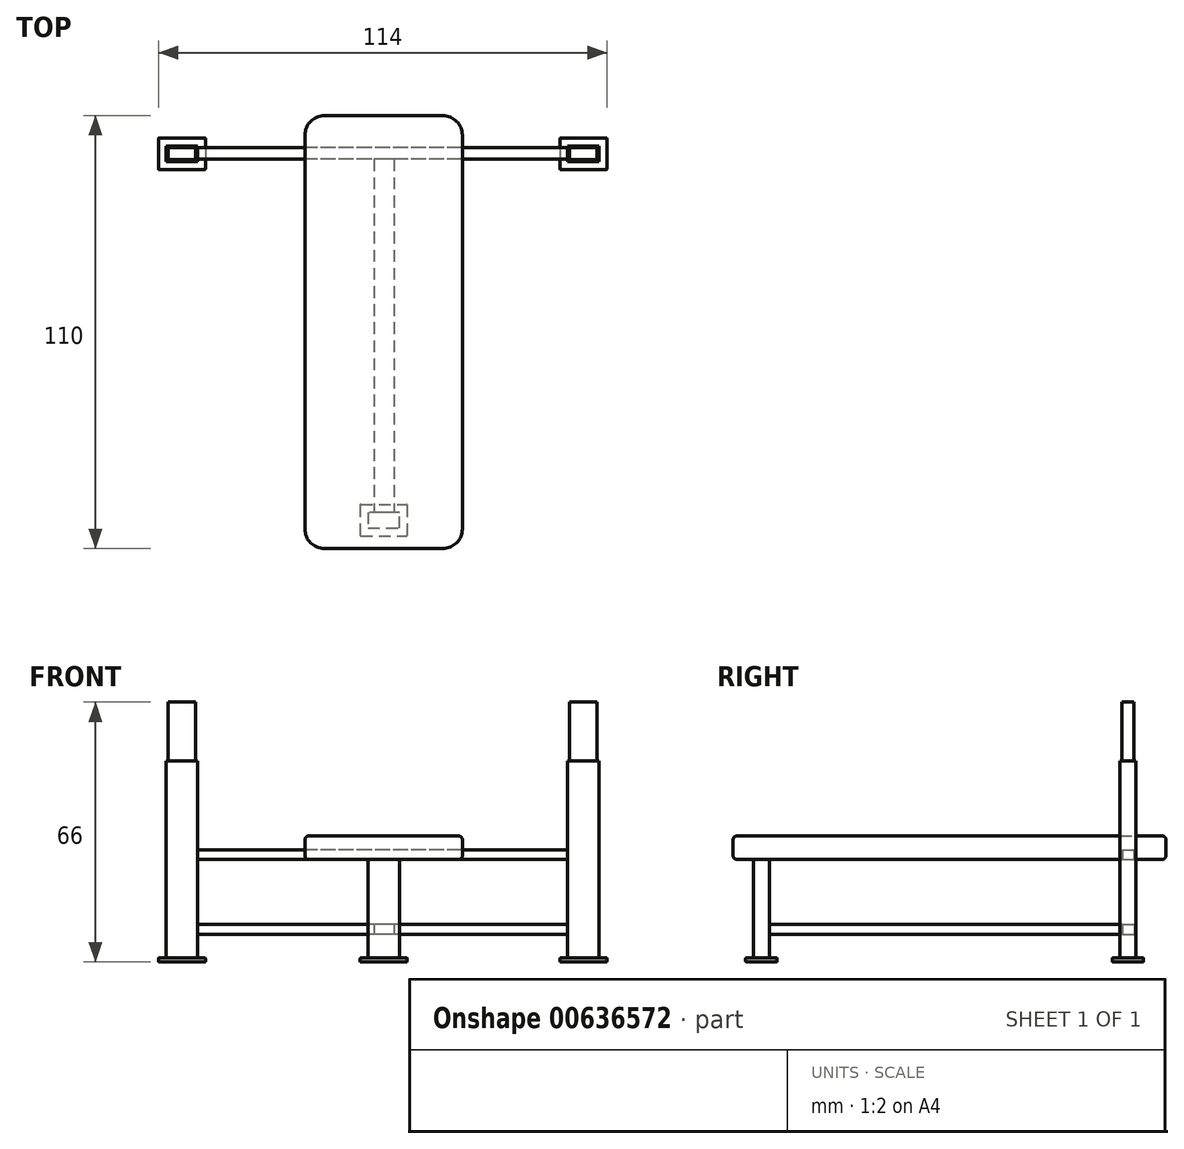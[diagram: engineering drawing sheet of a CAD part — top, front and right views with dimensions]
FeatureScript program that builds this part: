
annotation { "Feature Type Name" : "Feature", "Feature Type Description" : "" }
export const myFeature = defineFeature(function(context is Context, id is Id, definition is map)
    precondition{}
    {
        {
            var Q0;
            Q0=qCreatedBy(makeId("Top.planeOp"),FACE);
            var sketch = newSketch(context, id + "F0", { "sketchPlane" : qUnion([Q0])});
            skLineSegment(sketch, "E0.bottom", {"start": v(-5.75, -43.57) * mm, "end": v(6.25, -43.57) * mm});
            skLineSegment(sketch, "E0.top", {"start": v(-5.75, -51.57) * mm, "end": v(6.25, -51.57) * mm});
            skLineSegment(sketch, "E0.left", {"start": v(-5.75, -43.57) * mm, "end": v(-5.75, -51.57) * mm});
            skLineSegment(sketch, "E0.right", {"start": v(6.25, -43.57) * mm, "end": v(6.25, -51.57) * mm});
            skSolve(sketch);
        }
        {
            var Q0;
            Q0=qCreatedBy(makeId("Top.planeOp"),FACE);
            var sketch = newSketch(context, id + "F1", { "sketchPlane" : qUnion([Q0])});
            skLineSegment(sketch, "E1", {"start": v(0, 49.53) * mm, "end": v(0, -40.59) * mm, "construction": true});
            skLineSegment(sketch, "E2.bottom", {"start": v(45, 49.53) * mm, "end": v(57, 49.53) * mm});
            skLineSegment(sketch, "E2.top", {"start": v(45, 41.53) * mm, "end": v(57, 41.53) * mm});
            skLineSegment(sketch, "E2.left", {"start": v(45, 49.53) * mm, "end": v(45, 41.53) * mm});
            skLineSegment(sketch, "E2.right", {"start": v(57, 49.53) * mm, "end": v(57, 41.53) * mm});
            skLineSegment(sketch, "E3.bottom", {"start": v(-45, 49.53) * mm, "end": v(-57, 49.53) * mm});
            skLineSegment(sketch, "E3.top", {"start": v(-45, 41.53) * mm, "end": v(-57, 41.53) * mm});
            skLineSegment(sketch, "E3.left", {"start": v(-45, 49.53) * mm, "end": v(-45, 41.53) * mm});
            skLineSegment(sketch, "E3.right", {"start": v(-57, 49.53) * mm, "end": v(-57, 41.53) * mm});
            skSolve(sketch);
        }
        {
            var Q0;
            Q0 = qSketchRegion(id + "F1", true);
            var Q1;
            Q1 = qSketchRegion(id + "F0", true);
            extrude(context, id + "F2", {"entities" : qUnion([Q0, Q1]), "depth" : 1 * mm, "offsetDistance" : 25 * mm});
        }
        {
            var Q0;
            Q0=makeQuery(id+"F2.opExtrude","CAP_EDGE",EDGE,{"disambiguationData":[OSD([sQuery(id+"F0.wireOp",EDGE,"E0.left")])],"isStart":false});
            var Q1;
            Q1=makeQuery(id+"F2.opExtrude","CAP_EDGE",EDGE,{"disambiguationData":[OSD([sQuery(id+"F0.wireOp",EDGE,"E0.top")])],"isStart":false});
            var Q2;
            Q2=makeQuery(id+"F2.opExtrude","CAP_EDGE",EDGE,{"disambiguationData":[OSD([sQuery(id+"F0.wireOp",EDGE,"E0.top")])],"isStart":true});
            var Q3;
            Q3=makeQuery(id+"F2.opExtrude","SWEPT_EDGE",EDGE,{"disambiguationData":[OSD([sQuery(id+"F0.wireOp",EDGE,"E0.top"),sQuery(id+"F0.wireOp",EDGE,"E0.right")])]});
            var Q4;
            Q4=makeQuery(id+"F2.opExtrude","SWEPT_EDGE",EDGE,{"disambiguationData":[OSD([sQuery(id+"F0.wireOp",EDGE,"E0.top"),sQuery(id+"F0.wireOp",EDGE,"E0.left")])]});
            var Q5;
            Q5=makeQuery(id+"F2.opExtrude","CAP_EDGE",EDGE,{"disambiguationData":[OSD([sQuery(id+"F0.wireOp",EDGE,"E0.left")])],"isStart":true});
            var Q6;
            Q6=makeQuery(id+"F2.opExtrude","SWEPT_EDGE",EDGE,{"disambiguationData":[OSD([sQuery(id+"F0.wireOp",EDGE,"E0.bottom"),sQuery(id+"F0.wireOp",EDGE,"E0.left")])]});
            var Q7;
            Q7=makeQuery(id+"F2.opExtrude","CAP_EDGE",EDGE,{"disambiguationData":[OSD([sQuery(id+"F0.wireOp",EDGE,"E0.right")])],"isStart":false});
            var Q8;
            Q8=makeQuery(id+"F2.opExtrude","CAP_EDGE",EDGE,{"disambiguationData":[OSD([sQuery(id+"F0.wireOp",EDGE,"E0.right")])],"isStart":true});
            var Q9;
            Q9=makeQuery(id+"F2.opExtrude","CAP_EDGE",EDGE,{"disambiguationData":[OSD([sQuery(id+"F0.wireOp",EDGE,"E0.bottom")])],"isStart":false});
            var Q10;
            Q10=makeQuery(id+"F2.opExtrude","CAP_EDGE",EDGE,{"disambiguationData":[OSD([sQuery(id+"F0.wireOp",EDGE,"E0.bottom")])],"isStart":true});
            var Q11;
            Q11=makeQuery(id+"F2.opExtrude","SWEPT_EDGE",EDGE,{"disambiguationData":[OSD([sQuery(id+"F0.wireOp",EDGE,"E0.bottom"),sQuery(id+"F0.wireOp",EDGE,"E0.right")])]});
            var Q12;
            Q12=makeQuery(id+"F2.opExtrude","SWEPT_EDGE",EDGE,{"disambiguationData":[OSD([sQuery(id+"F1.wireOp",EDGE,"E3.top"),sQuery(id+"F1.wireOp",EDGE,"E3.left")])]});
            var Q13;
            Q13=makeQuery(id+"F2.opExtrude","CAP_EDGE",EDGE,{"disambiguationData":[OSD([sQuery(id+"F1.wireOp",EDGE,"E3.top")])],"isStart":true});
            var Q14;
            Q14=makeQuery(id+"F2.opExtrude","CAP_EDGE",EDGE,{"disambiguationData":[OSD([sQuery(id+"F1.wireOp",EDGE,"E3.top")])],"isStart":false});
            var Q15;
            Q15=makeQuery(id+"F2.opExtrude","SWEPT_EDGE",EDGE,{"disambiguationData":[OSD([sQuery(id+"F1.wireOp",EDGE,"E3.top"),sQuery(id+"F1.wireOp",EDGE,"E3.right")])]});
            var Q16;
            Q16=makeQuery(id+"F2.opExtrude","SWEPT_EDGE",EDGE,{"disambiguationData":[OSD([sQuery(id+"F1.wireOp",EDGE,"E3.bottom"),sQuery(id+"F1.wireOp",EDGE,"E3.left")])]});
            var Q17;
            Q17=makeQuery(id+"F2.opExtrude","CAP_EDGE",EDGE,{"disambiguationData":[OSD([sQuery(id+"F1.wireOp",EDGE,"E3.bottom")])],"isStart":false});
            var Q18;
            Q18=makeQuery(id+"F2.opExtrude","CAP_EDGE",EDGE,{"disambiguationData":[OSD([sQuery(id+"F1.wireOp",EDGE,"E3.right")])],"isStart":false});
            var Q19;
            Q19=makeQuery(id+"F2.opExtrude","CAP_EDGE",EDGE,{"disambiguationData":[OSD([sQuery(id+"F1.wireOp",EDGE,"E3.left")])],"isStart":false});
            var Q20;
            Q20=makeQuery(id+"F2.opExtrude","CAP_EDGE",EDGE,{"disambiguationData":[OSD([sQuery(id+"F1.wireOp",EDGE,"E3.right")])],"isStart":true});
            var Q21;
            Q21=makeQuery(id+"F2.opExtrude","SWEPT_EDGE",EDGE,{"disambiguationData":[OSD([sQuery(id+"F1.wireOp",EDGE,"E3.bottom"),sQuery(id+"F1.wireOp",EDGE,"E3.right")])]});
            var Q22;
            Q22=makeQuery(id+"F2.opExtrude","CAP_EDGE",EDGE,{"disambiguationData":[OSD([sQuery(id+"F1.wireOp",EDGE,"E3.left")])],"isStart":true});
            var Q23;
            Q23=makeQuery(id+"F2.opExtrude","CAP_EDGE",EDGE,{"disambiguationData":[OSD([sQuery(id+"F1.wireOp",EDGE,"E3.bottom")])],"isStart":true});
            var Q24;
            Q24=makeQuery(id+"F2.opExtrude","SWEPT_EDGE",EDGE,{"disambiguationData":[OSD([sQuery(id+"F1.wireOp",EDGE,"E2.top"),sQuery(id+"F1.wireOp",EDGE,"E2.right")])]});
            var Q25;
            Q25=makeQuery(id+"F2.opExtrude","CAP_EDGE",EDGE,{"disambiguationData":[OSD([sQuery(id+"F1.wireOp",EDGE,"E2.right")])],"isStart":false});
            var Q26;
            Q26=makeQuery(id+"F2.opExtrude","SWEPT_EDGE",EDGE,{"disambiguationData":[OSD([sQuery(id+"F1.wireOp",EDGE,"E2.bottom"),sQuery(id+"F1.wireOp",EDGE,"E2.right")])]});
            var Q27;
            Q27=makeQuery(id+"F2.opExtrude","CAP_EDGE",EDGE,{"disambiguationData":[OSD([sQuery(id+"F1.wireOp",EDGE,"E2.top")])],"isStart":false});
            var Q28;
            Q28=makeQuery(id+"F2.opExtrude","CAP_EDGE",EDGE,{"disambiguationData":[OSD([sQuery(id+"F1.wireOp",EDGE,"E2.top")])],"isStart":true});
            var Q29;
            Q29=makeQuery(id+"F2.opExtrude","CAP_EDGE",EDGE,{"disambiguationData":[OSD([sQuery(id+"F1.wireOp",EDGE,"E2.right")])],"isStart":true});
            var Q30;
            Q30=makeQuery(id+"F2.opExtrude","SWEPT_EDGE",EDGE,{"disambiguationData":[OSD([sQuery(id+"F1.wireOp",EDGE,"E2.top"),sQuery(id+"F1.wireOp",EDGE,"E2.left")])]});
            var Q31;
            Q31=makeQuery(id+"F2.opExtrude","CAP_EDGE",EDGE,{"disambiguationData":[OSD([sQuery(id+"F1.wireOp",EDGE,"E2.bottom")])],"isStart":false});
            var Q32;
            Q32=makeQuery(id+"F2.opExtrude","CAP_EDGE",EDGE,{"disambiguationData":[OSD([sQuery(id+"F1.wireOp",EDGE,"E2.left")])],"isStart":false});
            var Q33;
            Q33=makeQuery(id+"F2.opExtrude","SWEPT_FACE",FACE,{"disambiguationData":[OSD([sQuery(id+"F1.wireOp",EDGE,"E2.bottom")])]});
            var Q34;
            Q34=makeQuery(id+"F2.opExtrude","SWEPT_EDGE",EDGE,{"disambiguationData":[OSD([sQuery(id+"F1.wireOp",EDGE,"E2.bottom"),sQuery(id+"F1.wireOp",EDGE,"E2.left")])]});
            var Q35;
            Q35=makeQuery(id+"F2.opExtrude","CAP_EDGE",EDGE,{"disambiguationData":[OSD([sQuery(id+"F1.wireOp",EDGE,"E2.left")])],"isStart":true});
            fillet(context, id + "F3", {"entities" : qUnion([Q0, Q1, Q2, Q3, Q4, Q5, Q6, Q7, Q8, Q9, Q10, Q11, Q12, Q13, Q14, Q15, Q16, Q17, Q18, Q19, Q20, Q21, Q22, Q23, Q24, Q25, Q26, Q27, Q28, Q29, Q30, Q31, Q32, Q33, Q34, Q35]), "radius" : 0.2 * mm, "tangentPropagation" : true, "allowEdgeOverflow" : false});
        }
        {
            var Q0;
            Q0=makeQuery(id+"F2.opExtrude","CAP_FACE",FACE,{"disambiguationData":[OSD([sQuery(id+"F0.wireOp",EDGE,"E0.bottom"),sQuery(id+"F0.wireOp",EDGE,"E0.top"),sQuery(id+"F0.wireOp",EDGE,"E0.left"),sQuery(id+"F0.wireOp",EDGE,"E0.right")])],"isStart":false});
            var sketch = newSketch(context, id + "F4", { "sketchPlane" : qUnion([Q0])});
            skLineSegment(sketch, "E4.0", {"start": v(-3.75, -49.57) * mm, "end": v(4.25, -49.57) * mm});
            skLineSegment(sketch, "E4.1", {"start": v(-3.75, -45.57) * mm, "end": v(-3.75, -49.57) * mm});
            skLineSegment(sketch, "E4.2", {"start": v(4.25, -45.57) * mm, "end": v(-3.75, -45.57) * mm});
            skLineSegment(sketch, "E4.3", {"start": v(4.25, -49.57) * mm, "end": v(4.25, -45.57) * mm});
            skSolve(sketch);
        }
        {
            var Q0;
            Q0 = qSketchRegion(id + "F4", true);
            extrude(context, id + "F5", {"entities" : qUnion([Q0]), "operationType" : NewBodyOperationType.ADD, "depth" : 25 * mm, "offsetDistance" : 25 * mm});
        }
        {
            var Q0;
            Q0=makeQuery(id+"F2.opExtrude","CAP_FACE",FACE,{"disambiguationData":[OSD([sQuery(id+"F1.wireOp",EDGE,"E3.bottom"),sQuery(id+"F1.wireOp",EDGE,"E3.top"),sQuery(id+"F1.wireOp",EDGE,"E3.left"),sQuery(id+"F1.wireOp",EDGE,"E3.right")])],"isStart":false});
            var sketch = newSketch(context, id + "F6", { "sketchPlane" : qUnion([Q0])});
            skLineSegment(sketch, "E5.0", {"start": v(-47, 43.53) * mm, "end": v(-47, 47.53) * mm});
            skLineSegment(sketch, "E5.1", {"start": v(-55, 43.53) * mm, "end": v(-47, 43.53) * mm});
            skLineSegment(sketch, "E5.2", {"start": v(-55, 47.53) * mm, "end": v(-55, 43.53) * mm});
            skLineSegment(sketch, "E5.3", {"start": v(-47, 47.53) * mm, "end": v(-55, 47.53) * mm});
            skSolve(sketch);
        }
        {
            var Q0;
            Q0=makeQuery(id+"F6.imprint","IMPRINT",FACE,{"disambiguationData":[TD([[makeQuery(id+"F6.imprint","IMPRINT",EDGE,{"derivedFrom":sQuery(id+"F6.wireOp",EDGE,"E5.0")}),1.0]])]});
            extrude(context, id + "F7", {"entities" : qUnion([Q0]), "operationType" : NewBodyOperationType.ADD, "depth" : 50 * mm, "offsetDistance" : 25 * mm});
        }
        {
            var Q0;
            Q0=makeQuery(id+"F2.opExtrude","CAP_FACE",FACE,{"disambiguationData":[OSD([sQuery(id+"F1.wireOp",EDGE,"E2.bottom"),sQuery(id+"F1.wireOp",EDGE,"E2.top"),sQuery(id+"F1.wireOp",EDGE,"E2.left"),sQuery(id+"F1.wireOp",EDGE,"E2.right")])],"isStart":false});
            var sketch = newSketch(context, id + "F8", { "sketchPlane" : qUnion([Q0])});
            skLineSegment(sketch, "E6.0", {"start": v(47, 43.53) * mm, "end": v(55, 43.53) * mm});
            skLineSegment(sketch, "E6.1", {"start": v(47, 47.53) * mm, "end": v(47, 43.53) * mm});
            skLineSegment(sketch, "E6.2", {"start": v(55, 47.53) * mm, "end": v(47, 47.53) * mm});
            skLineSegment(sketch, "E6.3", {"start": v(55, 43.53) * mm, "end": v(55, 47.53) * mm});
            skSolve(sketch);
        }
        {
            var Q0;
            Q0=makeQuery(id+"F8.imprint","IMPRINT",FACE,{"disambiguationData":[TD([[makeQuery(id+"F8.imprint","IMPRINT",EDGE,{"derivedFrom":sQuery(id+"F8.wireOp",EDGE,"E6.0")}),1.0]])]});
            extrude(context, id + "F9", {"entities" : qUnion([Q0]), "operationType" : NewBodyOperationType.ADD, "depth" : 50 * mm, "offsetDistance" : 25 * mm});
        }
        {
            var Q0;
            Q0=makeQuery(id+"F7.opExtrude","SWEPT_FACE",FACE,{"disambiguationData":[OSD([sQuery(id+"F6.wireOp",EDGE,"E5.0")])]});
            var sketch = newSketch(context, id + "F10", { "sketchPlane" : qUnion([Q0])});
            skLineSegment(sketch, "E7.bottom", {"start": v(44.1, 9.5) * mm, "end": v(47.1, 9.5) * mm});
            skLineSegment(sketch, "E7.top", {"start": v(44.1, 7) * mm, "end": v(47.1, 7) * mm});
            skLineSegment(sketch, "E7.left", {"start": v(44.1, 9.5) * mm, "end": v(44.1, 7) * mm});
            skLineSegment(sketch, "E7.right", {"start": v(47.1, 9.5) * mm, "end": v(47.1, 7) * mm});
            skSolve(sketch);
        }
        {
            var Q0;
            Q0 = qSketchRegion(id + "F10", true);
            extrude(context, id + "F11", {"entities" : qUnion([Q0]), "endBound" : BoundingType.UP_TO_NEXT, "depth" : 25 * mm, "offsetDistance" : 25 * mm});
        }
        {
            var Q0;
            Q0=makeQuery(id+"F5.opExtrude","SWEPT_FACE",FACE,{"disambiguationData":[OSD([sQuery(id+"F4.wireOp",EDGE,"E4.2")])]});
            var sketch = newSketch(context, id + "F12", { "sketchPlane" : qUnion([Q0])});
            skLineSegment(sketch, "E8.bottom", {"start": v(-2.85, 9.5) * mm, "end": v(2.15, 9.5) * mm});
            skLineSegment(sketch, "E8.top", {"start": v(-2.85, 7) * mm, "end": v(2.15, 7) * mm});
            skLineSegment(sketch, "E8.left", {"start": v(-2.85, 9.5) * mm, "end": v(-2.85, 7) * mm});
            skLineSegment(sketch, "E8.right", {"start": v(2.15, 9.5) * mm, "end": v(2.15, 7) * mm});
            skSolve(sketch);
        }
        {
            var Q0;
            Q0 = qSketchRegion(id + "F12", true);
            extrude(context, id + "F13", {"entities" : qUnion([Q0]), "endBound" : BoundingType.UP_TO_NEXT, "depth" : 25 * mm, "offsetDistance" : 25 * mm});
        }
        {
            var Q0;
            Q0=makeQuery(id+"F7.opExtrude","SWEPT_FACE",FACE,{"disambiguationData":[OSD([sQuery(id+"F6.wireOp",EDGE,"E5.0")])]});
            var sketch = newSketch(context, id + "F14", { "sketchPlane" : qUnion([Q0])});
            skLineSegment(sketch, "E9.bottom", {"start": v(44.1, 28.5) * mm, "end": v(47.1, 28.5) * mm});
            skLineSegment(sketch, "E9.top", {"start": v(44.1, 26) * mm, "end": v(47.1, 26) * mm});
            skLineSegment(sketch, "E9.left", {"start": v(44.1, 28.5) * mm, "end": v(44.1, 26) * mm});
            skLineSegment(sketch, "E9.right", {"start": v(47.1, 28.5) * mm, "end": v(47.1, 26) * mm});
            skSolve(sketch);
        }
        {
            var Q0;
            Q0 = qSketchRegion(id + "F14", true);
            extrude(context, id + "F15", {"entities" : qUnion([Q0]), "endBound" : BoundingType.UP_TO_NEXT, "depth" : 25 * mm, "offsetDistance" : 25 * mm});
        }
        {
            var Q0;
            Q0=makeQuery(id+"F5.opExtrude","CAP_FACE",FACE,{"disambiguationData":[OSD([sQuery(id+"F4.wireOp",EDGE,"E4.0"),sQuery(id+"F4.wireOp",EDGE,"E4.1"),sQuery(id+"F4.wireOp",EDGE,"E4.2"),sQuery(id+"F4.wireOp",EDGE,"E4.3")])],"isStart":false});
            var sketch = newSketch(context, id + "F16", { "sketchPlane" : qUnion([Q0])});
            skSolve(sketch);
        }
        {
            var Q0;
            Q0=makeQuery(id+"F16.imprint","IMPRINT",FACE,{"disambiguationData":[TD([[makeQuery(id+"F16.imprint","IMPRINT",EDGE,{"derivedFrom":makeQuery(id+"F5.opExtrude","CAP_EDGE",EDGE,{"disambiguationData":[OSD([sQuery(id+"F4.wireOp",EDGE,"E4.0")])],"isStart":false})}),1.0]])]});
            var sketch = newSketch(context, id + "F17", { "sketchPlane" : qUnion([Q0])});
            skLineSegment(sketch, "E10.bottom", {"start": v(20.24, -54.79) * mm, "end": v(-19.76, -54.79) * mm});
            skLineSegment(sketch, "E10.top", {"start": v(20.24, 55.21) * mm, "end": v(-19.76, 55.21) * mm});
            skLineSegment(sketch, "E10.left", {"start": v(20.24, -54.79) * mm, "end": v(20.24, 55.21) * mm});
            skLineSegment(sketch, "E10.right", {"start": v(-19.76, -54.79) * mm, "end": v(-19.76, 55.21) * mm});
            skLineSegment(sketch, "E11", {"start": v(0, 60.76) * mm, "end": v(0, -66.65) * mm, "construction": true});
            skSolve(sketch);
        }
        {
            var Q0;
            Q0 = qSketchRegion(id + "F16", true);
            var Q1;
            Q1 = qSketchRegion(id + "F17", true);
            extrude(context, id + "F18", {"entities" : qUnion([Q0, Q1]), "depth" : 6 * mm, "offsetDistance" : 25 * mm});
        }
        {
            var Q0;
            Q0=makeQuery(id+"F18.opExtrude","CAP_EDGE",EDGE,{"disambiguationData":[OSD([sQuery(id+"F17.wireOp",EDGE,"E10.top")])],"isStart":false});
            var Q1;
            Q1=makeQuery(id+"F18.opExtrude","CAP_EDGE",EDGE,{"disambiguationData":[OSD([sQuery(id+"F17.wireOp",EDGE,"E10.top")])],"isStart":true});
            var Q2;
            Q2=makeQuery(id+"F18.opExtrude","CAP_EDGE",EDGE,{"disambiguationData":[OSD([sQuery(id+"F17.wireOp",EDGE,"E10.left")])],"isStart":false});
            var Q3;
            Q3=makeQuery(id+"F18.opExtrude","CAP_EDGE",EDGE,{"disambiguationData":[OSD([sQuery(id+"F17.wireOp",EDGE,"E10.left")])],"isStart":true});
            var Q4;
            Q4=makeQuery(id+"F18.opExtrude","CAP_EDGE",EDGE,{"disambiguationData":[OSD([sQuery(id+"F17.wireOp",EDGE,"E10.bottom")])],"isStart":false});
            var Q5;
            Q5=makeQuery(id+"F18.opExtrude","CAP_EDGE",EDGE,{"disambiguationData":[OSD([sQuery(id+"F17.wireOp",EDGE,"E10.right")])],"isStart":false});
            var Q6;
            Q6=makeQuery(id+"F18.opExtrude","CAP_EDGE",EDGE,{"disambiguationData":[OSD([sQuery(id+"F17.wireOp",EDGE,"E10.right")])],"isStart":true});
            var Q7;
            Q7=makeQuery(id+"F18.opExtrude","CAP_EDGE",EDGE,{"disambiguationData":[OSD([sQuery(id+"F17.wireOp",EDGE,"E10.bottom")])],"isStart":true});
            fillet(context, id + "F19", {"entities" : qUnion([Q0, Q1, Q2, Q3, Q4, Q5, Q6, Q7]), "radius" : 1 * mm, "tangentPropagation" : true, "allowEdgeOverflow" : false});
        }
        {
            var Q0;
            Q0=makeQuery(id+"F18.opExtrude","SWEPT_EDGE",EDGE,{"disambiguationData":[OSD([sQuery(id+"F17.wireOp",EDGE,"E10.top"),sQuery(id+"F17.wireOp",EDGE,"E10.right")])]});
            var Q1;
            Q1=makeQuery(id+"F18.opExtrude","SWEPT_EDGE",EDGE,{"disambiguationData":[OSD([sQuery(id+"F17.wireOp",EDGE,"E10.top"),sQuery(id+"F17.wireOp",EDGE,"E10.left")])]});
            var Q2;
            Q2=makeQuery(id+"F18.opExtrude","SWEPT_EDGE",EDGE,{"disambiguationData":[OSD([sQuery(id+"F17.wireOp",EDGE,"E10.bottom"),sQuery(id+"F17.wireOp",EDGE,"E10.right")])]});
            var Q3;
            Q3=makeQuery(id+"F18.opExtrude","SWEPT_EDGE",EDGE,{"disambiguationData":[OSD([sQuery(id+"F17.wireOp",EDGE,"E10.bottom"),sQuery(id+"F17.wireOp",EDGE,"E10.left")])]});
            fillet(context, id + "F20", {"entities" : qUnion([Q0, Q1, Q2, Q3]), "radius" : 5 * mm, "tangentPropagation" : true, "allowEdgeOverflow" : false});
        }
        {
            var Q0;
            Q0=makeQuery(id+"F7.opExtrude","CAP_FACE",FACE,{"disambiguationData":[OSD([sQuery(id+"F6.wireOp",EDGE,"E5.0"),sQuery(id+"F6.wireOp",EDGE,"E5.1"),sQuery(id+"F6.wireOp",EDGE,"E5.2"),sQuery(id+"F6.wireOp",EDGE,"E5.3")])],"isStart":false});
            var sketch = newSketch(context, id + "F21", { "sketchPlane" : qUnion([Q0])});
            skLineSegment(sketch, "E12.0", {"start": v(-47.5, 44.03) * mm, "end": v(-47.5, 47.03) * mm});
            skLineSegment(sketch, "E12.1", {"start": v(-54.5, 44.03) * mm, "end": v(-47.5, 44.03) * mm});
            skLineSegment(sketch, "E12.2", {"start": v(-54.5, 47.03) * mm, "end": v(-54.5, 44.03) * mm});
            skLineSegment(sketch, "E12.3", {"start": v(-47.5, 47.03) * mm, "end": v(-54.5, 47.03) * mm});
            skLineSegment(sketch, "E13.0", {"start": v(47.5, 44.03) * mm, "end": v(54.5, 44.03) * mm});
            skLineSegment(sketch, "E13.1", {"start": v(47.5, 47.03) * mm, "end": v(47.5, 44.03) * mm});
            skLineSegment(sketch, "E13.2", {"start": v(54.5, 47.03) * mm, "end": v(47.5, 47.03) * mm});
            skLineSegment(sketch, "E13.3", {"start": v(54.5, 44.03) * mm, "end": v(54.5, 47.03) * mm});
            skSolve(sketch);
        }
        {
            var Q0;
            Q0 = qSketchRegion(id + "F21", true);
            extrude(context, id + "F22", {"entities" : qUnion([Q0]), "depth" : 15 * mm, "offsetDistance" : 25 * mm});
        }
    });
